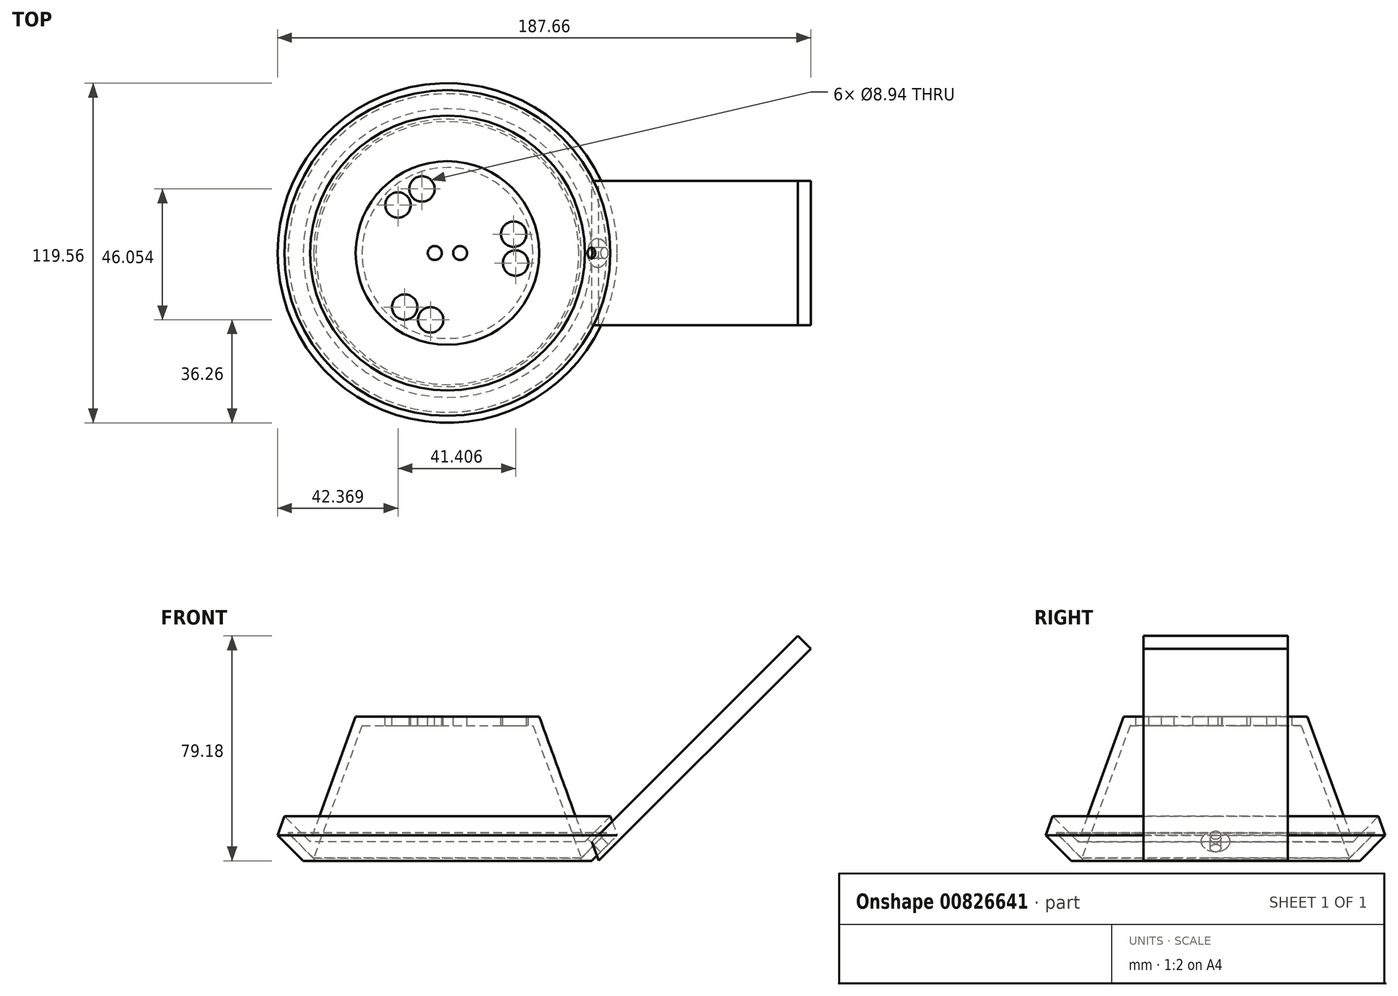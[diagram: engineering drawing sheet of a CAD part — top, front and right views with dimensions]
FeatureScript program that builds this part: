
annotation { "Feature Type Name" : "Feature", "Feature Type Description" : "" }
export const myFeature = defineFeature(function(context is Context, id is Id, definition is map)
    precondition{}
    {
        {
            var Q0;
            Q0=qCreatedBy(makeId("Front.planeOp"),FACE);
            var sketch = newSketch(context, id + "F0", { "sketchPlane" : qUnion([Q0])});
            skLineSegment(sketch, "E0", {"start": v(32.3, 94.92) * mm, "end": v(48.37, 50.8) * mm});
            skLineSegment(sketch, "E1", {"start": v(48.37, 50.8) * mm, "end": v(57.35, 59.78) * mm});
            skLineSegment(sketch, "E2", {"start": v(57.35, 59.78) * mm, "end": v(59.78, 53.1) * mm});
            skLineSegment(sketch, "E3", {"start": v(59.78, 53.1) * mm, "end": v(50.8, 44.12) * mm});
            skLineSegment(sketch, "E4", {"start": v(0, 53.57) * mm, "end": v(0, 0) * mm});
            skLineSegment(sketch, "E5", {"start": v(32.3, 94.92) * mm, "end": v(0, 94.92) * mm});
            skLineSegment(sketch, "E6", {"start": v(0, 94.92) * mm, "end": v(0, 44.12) * mm});
            skLineSegment(sketch, "E7", {"start": v(0, 44.12) * mm, "end": v(50.8, 44.12) * mm});
            skSolve(sketch);
        }
        {
            var Q0;
            Q0=makeQuery(id+"F0.imprint","IMPRINT",FACE,{"disambiguationData":[TD([[makeQuery(id+"F0.imprint","IMPRINT",EDGE,{"derivedFrom":sQuery(id+"F0.wireOp",EDGE,"E0")}),-1.0]])]});
            var Q1;
            {var subQ0=sQuery(id+"F0.wireOp",EDGE,"E1");Q1=makeQuery(id+"F0.imprint","IMPRINT",FACE,{"disambiguationData":[TD([[makeQuery(id+"F0.imprint","IMPRINT",EDGE,{"derivedFrom":subQ0}),-1.0]])]});}
            var Q2;
            Q2=sQuery(id+"F0.wireOp",EDGE,"E4");
            revolve(context, id + "F1", {"surfaceOperationType" : NewSurfaceOperationType.NEW, "entities" : qUnion([Q0, Q1]), "axis" : qUnion([Q2]), "revolveType" : RevolveType.FULL});
        }
        {
            var Q0;
            Q0=qCreatedBy(makeId("Front.planeOp"),FACE);
            var sketch = newSketch(context, id + "F2", { "sketchPlane" : qUnion([Q0])});
            skLineSegment(sketch, "E8.0", {"start": v(127.88, 118.72) * mm, "end": v(53.3, 44.14) * mm});
            skLineSegment(sketch, "E8.1", {"start": v(50.8, 50.8) * mm, "end": v(123.3, 123.3) * mm});
            skLineSegment(sketch, "E8.2", {"start": v(123.3, 123.3) * mm, "end": v(127.88, 118.72) * mm});
            skPoint(sketch, "E8.3", {"position": v(125.59, 121) * mm});
            skLineSegment(sketch, "E9", {"start": v(50.8, 50.8) * mm, "end": v(53.3, 44.14) * mm});
            skSolve(sketch);
        }
        {
            var Q0;
            Q0=makeQuery(id+"F2.imprint","IMPRINT",FACE,{"disambiguationData":[TD([[makeQuery(id+"F2.imprint","IMPRINT",EDGE,{"derivedFrom":sQuery(id+"F2.wireOp",EDGE,"E8.0")}),-1.0]])]});
            extrude(context, id + "F3", {"entities" : qUnion([Q0]), "depth" : 25.4 * mm, "offsetDistance" : 25.4 * mm, "hasSecondDirection" : true, "secondDirectionOppositeDirection" : true, "secondDirectionDepth" : 25.4 * mm});
        }
        {
            var Q0;
            Q0=makeQuery(id+"F3.opExtrude","SWEPT_FACE",FACE,{"disambiguationData":[OSD([sQuery(id+"F2.wireOp",EDGE,"E8.1")])]});
            var sketch = newSketch(context, id + "F4", { "sketchPlane" : qUnion([Q0])});
            skEllipse(sketch, "E10.0", {"center": v(0, 35.92) * mm, "majorRadius": 48.37 * mm, "minorRadius": 34.2 * mm, "majorAxis": v(-1, 0), "construction": true});
            skEllipse(sketch, "E10.1", {"center": v(0, 42.27) * mm, "majorRadius": 57.35 * mm, "minorRadius": 40.55 * mm, "majorAxis": v(-1, 0), "construction": true});
            skLineSegment(sketch, "E11", {"start": v(0, 64.03) * mm, "end": v(0, 82.82) * mm, "construction": true});
            skCircle(sketch, "E12", {"center": v(0, 73.42) * mm, "radius": 1.9 * mm});
            skSolve(sketch);
        }
        {
            var Q0;
            Q0=qSketchRegion(id+"F4",true);
            extrude(context, id + "F5", {"entities" : qUnion([Q0]), "operationType" : NewBodyOperationType.REMOVE, "endBound" : BoundingType.UP_TO_NEXT, "oppositeDirection" : true, "depth" : 25.4 * mm, "offsetDistance" : 25.4 * mm, "hasSecondDirection" : true, "secondDirectionBound" : SecondDirectionBoundingType.UP_TO_NEXT, "secondDirectionOppositeDirection" : false, "secondDirectionDepth" : 25.4 * mm});
        }
        {
            var Q0;
            Q0=makeQuery(id+"F1.opRevolve","SWEPT_FACE",FACE,{"disambiguationData":[OSD([sQuery(id+"F0.wireOp",EDGE,"E7")])]});
            shell(context, id + "F6", {"entities" : qUnion([Q0]), "thickness" : 3.17 * mm});
        }
        {
            var Q0;
            Q0=makeQuery(id+"F1.opRevolve","SWEPT_FACE",FACE,{"disambiguationData":[OSD([sQuery(id+"F0.wireOp",EDGE,"E5")])]});
            var sketch = newSketch(context, id + "F7", { "sketchPlane" : qUnion([Q0])});
            skCircle(sketch, "E13", {"center": v(-4.46, 0) * mm, "radius": 2.47 * mm});
            skCircle(sketch, "E14", {"center": v(4.47, 0) * mm, "radius": 2.47 * mm});
            skSolve(sketch);
        }
        {
            var Q0;
            Q0=qSketchRegion(id+"F7",true);
            extrude(context, id + "F8", {"entities" : qUnion([Q0]), "operationType" : NewBodyOperationType.REMOVE, "endBound" : BoundingType.UP_TO_NEXT, "oppositeDirection" : true, "depth" : 25.4 * mm, "offsetDistance" : 25.4 * mm});
        }
        {
            var Q0;
            Q0=makeQuery(id+"F1.opRevolve","SWEPT_FACE",FACE,{"disambiguationData":[OSD([sQuery(id+"F0.wireOp",EDGE,"E5")])]});
            var sketch = newSketch(context, id + "F9", { "sketchPlane" : qUnion([Q0])});
            skLineSegment(sketch, "E15", {"start": v(0, 0) * mm, "end": v(-17.97, 26.85) * mm, "construction": true});
            skLineSegment(sketch, "E16", {"start": v(0, 0) * mm, "end": v(32.24, 2.14) * mm, "construction": true});
            skLineSegment(sketch, "E17", {"start": v(0, 0) * mm, "end": v(-14.27, -28.99) * mm, "construction": true});
            skCircle(sketch, "E18", {"center": v(0, 0) * mm, "radius": 24.25 * mm, "construction": true});
            skCircle(sketch, "E19", {"center": v(23.33, 6.64) * mm, "radius": 4.47 * mm});
            skCircle(sketch, "E20", {"center": v(24, -3.52) * mm, "radius": 4.47 * mm});
            skCircle(sketch, "E21", {"center": v(-5.92, -23.52) * mm, "radius": 4.47 * mm});
            skCircle(sketch, "E22", {"center": v(-15.03, -19.03) * mm, "radius": 4.47 * mm});
            skCircle(sketch, "E23", {"center": v(-8.97, 22.53) * mm, "radius": 4.47 * mm});
            skCircle(sketch, "E24", {"center": v(-17.41, 16.88) * mm, "radius": 4.47 * mm});
            skSolve(sketch);
        }
        {
            var Q0;
            Q0=makeQuery(id+"F9.imprint","IMPRINT",FACE,{"disambiguationData":[TD([[makeQuery(id+"F9.imprint","IMPRINT",EDGE,{"derivedFrom":sQuery(id+"F9.wireOp",EDGE,"E24")}),1.0]])]});
            var Q1;
            Q1=makeQuery(id+"F9.imprint","IMPRINT",FACE,{"disambiguationData":[TD([[makeQuery(id+"F9.imprint","IMPRINT",EDGE,{"derivedFrom":sQuery(id+"F9.wireOp",EDGE,"E23")}),1.0]])]});
            var Q2;
            Q2=makeQuery(id+"F9.imprint","IMPRINT",FACE,{"disambiguationData":[TD([[makeQuery(id+"F9.imprint","IMPRINT",EDGE,{"derivedFrom":sQuery(id+"F9.wireOp",EDGE,"E19")}),1.0]])]});
            var Q3;
            Q3=makeQuery(id+"F9.imprint","IMPRINT",FACE,{"disambiguationData":[TD([[makeQuery(id+"F9.imprint","IMPRINT",EDGE,{"derivedFrom":sQuery(id+"F9.wireOp",EDGE,"E20")}),1.0]])]});
            var Q4;
            Q4=makeQuery(id+"F9.imprint","IMPRINT",FACE,{"disambiguationData":[TD([[makeQuery(id+"F9.imprint","IMPRINT",EDGE,{"derivedFrom":sQuery(id+"F9.wireOp",EDGE,"E21")}),1.0]])]});
            var Q5;
            Q5=makeQuery(id+"F9.imprint","IMPRINT",FACE,{"disambiguationData":[TD([[makeQuery(id+"F9.imprint","IMPRINT",EDGE,{"derivedFrom":sQuery(id+"F9.wireOp",EDGE,"E22")}),1.0]])]});
            extrude(context, id + "F10", {"entities" : qUnion([Q0, Q1, Q2, Q3, Q4, Q5]), "operationType" : NewBodyOperationType.REMOVE, "endBound" : BoundingType.UP_TO_NEXT, "oppositeDirection" : true, "depth" : 25.4 * mm, "offsetDistance" : 25.4 * mm});
        }
    });
